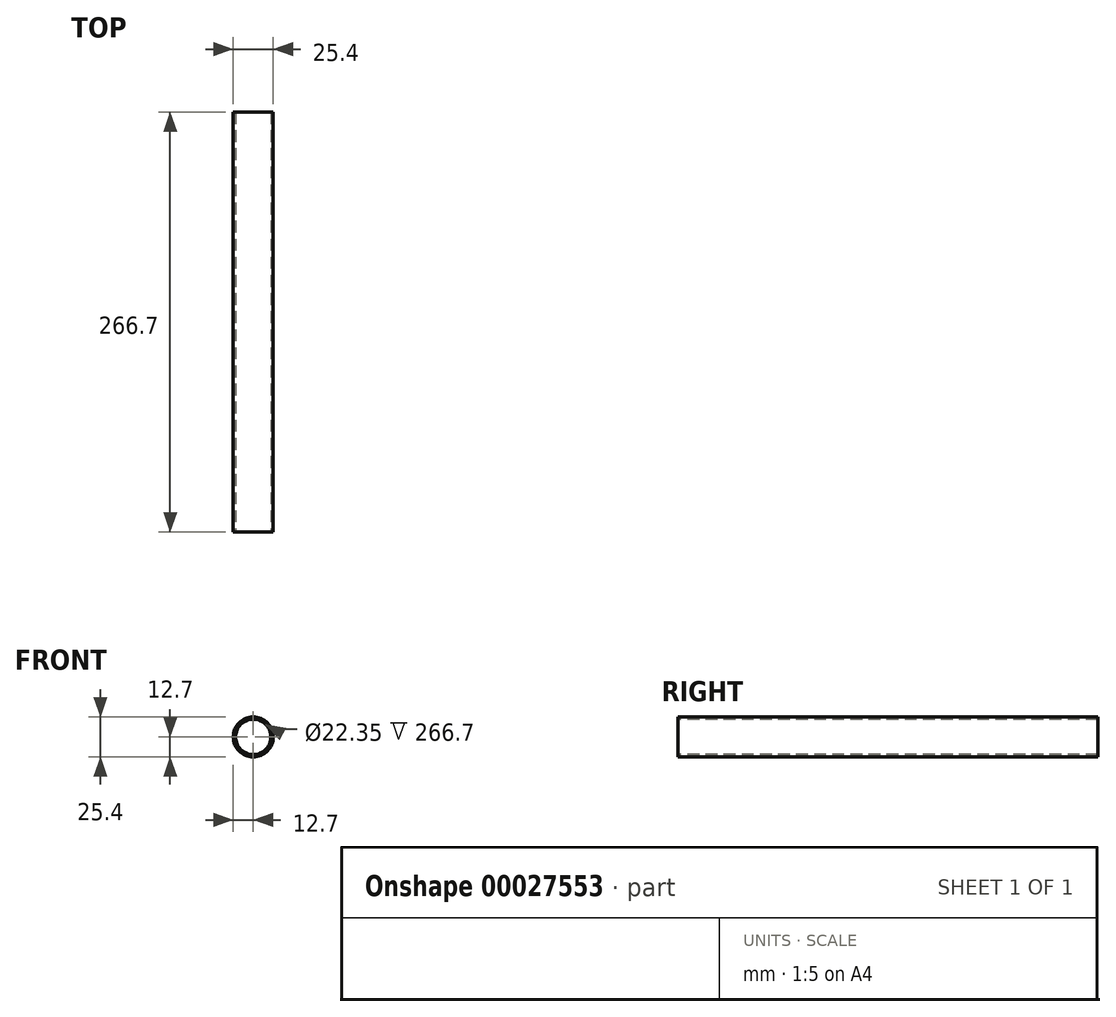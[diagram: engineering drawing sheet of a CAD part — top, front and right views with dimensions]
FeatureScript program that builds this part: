
annotation { "Feature Type Name" : "Feature", "Feature Type Description" : "" }
export const myFeature = defineFeature(function(context is Context, id is Id, definition is map)
    precondition{}
    {
        {
            var Q0;
            Q0=qCreatedBy(makeId("Front.planeOp"),FACE);
            var sketch = newSketch(context, id + "F0", { "sketchPlane" : qUnion([Q0])});
            skCircle(sketch, "E0", {"center": v(0, 0) * mm, "radius": 12.7 * mm});
            skSolve(sketch);
        }
        {
            var Q0;
            Q0 = qSketchRegion(id + "F0", true);
            extrude(context, id + "F1", {"entities" : qUnion([Q0]), "oppositeDirection" : true, "depth" : 266.7 * mm});
        }
        {
            var Q0;
            Q0=makeQuery(id+"F1.opExtrude","CAP_FACE",FACE,{"disambiguationData":[OSD([sQuery(id+"F0.wireOp",EDGE,"E0")])],"isStart":true});
            var sketch = newSketch(context, id + "F2", { "sketchPlane" : qUnion([Q0])});
            skCircle(sketch, "E1.0", {"center": v(0, 0) * mm, "radius": 11.18 * mm});
            skSolve(sketch);
        }
        {
            var Q0;
            Q0 = qSketchRegion(id + "F2", true);
            var Q1;
            Q1=makeQuery(id+"F1.opExtrude","CAP_FACE",FACE,{"disambiguationData":[OSD([sQuery(id+"F0.wireOp",EDGE,"E0")])],"isStart":false});
            extrude(context, id + "F3", {"entities" : qUnion([Q0]), "operationType" : NewBodyOperationType.REMOVE, "endBound" : BoundingType.UP_TO_SURFACE, "oppositeDirection" : true, "endBoundEntityFace" : qUnion([Q1]), "depth" : 25.4 * mm});
        }
    });
